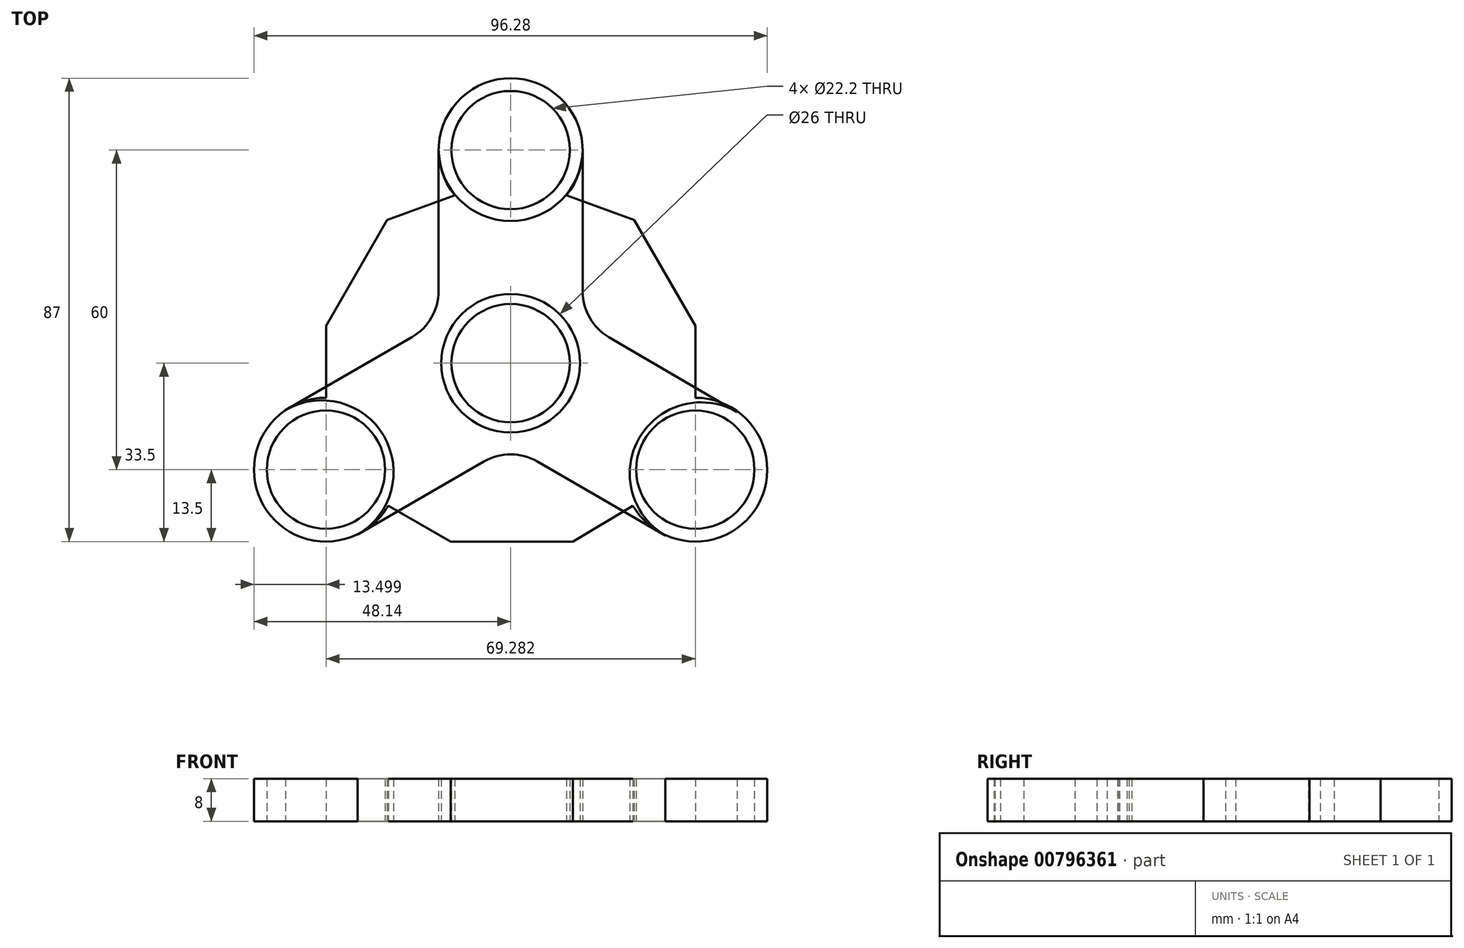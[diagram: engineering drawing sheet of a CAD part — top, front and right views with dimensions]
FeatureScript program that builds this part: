
annotation { "Feature Type Name" : "Feature", "Feature Type Description" : "" }
export const myFeature = defineFeature(function(context is Context, id is Id, definition is map)
    precondition{}
    {
        {
            var Q0;
            Q0=qCreatedBy(makeId("Top.planeOp"),FACE);
            var sketch = newSketch(context, id + "F0", { "sketchPlane" : qUnion([Q0])});
            skCircle(sketch, "E0", {"center": v(0, 0) * mm, "radius": 13.5 * mm});
            skCircle(sketch, "E1", {"center": v(0, 40) * mm, "radius": 13.5 * mm});
            skCircle(sketch, "E2.1.0", {"center": v(-34.64, -20) * mm, "radius": 13.5 * mm});
            skCircle(sketch, "E2.2.0", {"center": v(34.64, -20) * mm, "radius": 13.5 * mm});
            skCircle(sketch, "E3", {"center": v(0, 40) * mm, "radius": 11.1 * mm});
            skCircle(sketch, "E4", {"center": v(34.64, -20) * mm, "radius": 11.1 * mm});
            skCircle(sketch, "E5", {"center": v(-34.64, -20) * mm, "radius": 11.1 * mm});
            skCircle(sketch, "E6", {"center": v(0, 0) * mm, "radius": 11.1 * mm});
            skLineSegment(sketch, "E7", {"start": v(-34.64, 7) * mm, "end": v(-23.17, 26.88) * mm});
            skLineSegment(sketch, "E8", {"start": v(23.17, 26.88) * mm, "end": v(34.64, 7) * mm});
            skLineSegment(sketch, "E9", {"start": v(-11.26, -33.5) * mm, "end": v(11.7, -33.5) * mm});
            skLineSegment(sketch, "E10", {"start": v(-34.64, 7) * mm, "end": v(-34.64, -6.5) * mm});
            skLineSegment(sketch, "E11", {"start": v(-22.95, -26.75) * mm, "end": v(-11.26, -33.5) * mm});
            skPoint(sketch, "E12.orphan", {"position": v(-46.33, -13.25) * mm});
            skLineSegment(sketch, "E13", {"start": v(34.64, 7) * mm, "end": v(34.64, -6.5) * mm});
            skLineSegment(sketch, "E14", {"start": v(22.95, -26.75) * mm, "end": v(11.7, -33.5) * mm});
            skPoint(sketch, "E15.orphan", {"position": v(34.64, -33.5) * mm});
            skLineSegment(sketch, "E16", {"start": v(-10.48, 31.49) * mm, "end": v(-23.17, 26.87) * mm});
            skPoint(sketch, "E17.orphan", {"position": v(-11.7, 46.75) * mm});
            skLineSegment(sketch, "E18", {"start": v(10.48, 31.49) * mm, "end": v(23.17, 26.88) * mm});
            skPoint(sketch, "E19.orphan", {"position": v(11.7, 46.75) * mm});
            skSolve(sketch);
        }
        {
            var Q0;
            Q0=qCreatedBy(makeId("Top.planeOp"),FACE);
            var sketch = newSketch(context, id + "F1", { "sketchPlane" : qUnion([Q0])});
            skLineSegment(sketch, "E20", {"start": v(-42.2, -8.78) * mm, "end": v(-18.5, 4.9) * mm});
            skLineSegment(sketch, "E21", {"start": v(-28.7, -32.16) * mm, "end": v(-5, -18.48) * mm});
            skLineSegment(sketch, "E22", {"start": v(18.46, 4.86) * mm, "end": v(42.5, -9.18) * mm});
            skLineSegment(sketch, "E23", {"start": v(29.04, -32.36) * mm, "end": v(5, -18.48) * mm});
            skLineSegment(sketch, "E24", {"start": v(-13.5, 40.18) * mm, "end": v(-13.5, 13.57) * mm});
            skLineSegment(sketch, "E25", {"start": v(13.5, 40.18) * mm, "end": v(13.5, 13.5) * mm});
            skPoint(sketch, "E26.orphan", {"position": v(-13.5, 0) * mm});
            skPoint(sketch, "E27.orphan", {"position": v(13.5, 0) * mm});
            skPoint(sketch, "E28.visualSharp", {"position": v(-13.5, 7.8) * mm});
            skArc(sketch, "E28.filletArc", {"start": v(-18.5, 4.9) * mm, "mid": v(-14.84, 8.57) * mm, "end": v(-13.5, 13.57) * mm});
            skPoint(sketch, "E29.visualSharp", {"position": v(13.5, 7.75) * mm});
            skArc(sketch, "E29.filletArc", {"start": v(13.5, 13.5) * mm, "mid": v(14.83, 8.51) * mm, "end": v(18.46, 4.86) * mm});
            skPoint(sketch, "E30.visualSharp", {"position": v(0, -15.59) * mm});
            skArc(sketch, "E30.filletArc", {"start": v(5, -18.48) * mm, "mid": v(0, -17.14) * mm, "end": v(-5, -18.48) * mm});
            skArc(sketch, "E31", {"start": v(-13.5, 40.18) * mm, "mid": v(0, 26.68) * mm, "end": v(13.5, 40.18) * mm});
            skPoint(sketch, "E31.third.point", {"position": v(0, 53.68) * mm});
            skPoint(sketch, "E31.third.point.positionSnap0", {"position": v(0, 40.18) * mm});
            skArc(sketch, "E32", {"start": v(42.5, -9.18) * mm, "mid": v(24.15, -14.02) * mm, "end": v(29.04, -32.36) * mm});
            skPoint(sketch, "E32.third.point", {"position": v(47.1, -27.85) * mm});
            skArc(sketch, "E33", {"start": v(-28.7, -32.16) * mm, "mid": v(-23.77, -13.72) * mm, "end": v(-42.2, -8.78) * mm});
            skPoint(sketch, "E33.third.point", {"position": v(-48.06, -25.32) * mm});
            skPoint(sketch, "E33.third.point.positionSnap0", {"position": v(-16.85, -25.32) * mm});
            skCircle(sketch, "E34", {"center": v(0, 0) * mm, "radius": 13 * mm});
            skSolve(sketch);
        }
        {
            var Q0;
            Q0=makeQuery(id+"F1.imprint","IMPRINT",FACE,{"disambiguationData":[TD([[makeQuery(id+"F1.imprint","IMPRINT",EDGE,{"derivedFrom":sQuery(id+"F1.wireOp",EDGE,"E20")}),-1.0]])]});
            extrude(context, id + "F2", {"entities" : qUnion([Q0]), "endBound" : BoundingType.SYMMETRIC, "depth" : 8 * mm, "offsetDistance" : 25 * mm});
        }
        {
            var Q0;
            Q0=makeQuery(id+"F0.imprint","IMPRINT",FACE,{"disambiguationData":[TD([[makeQuery(id+"F0.imprint","IMPRINT",EDGE,{"derivedFrom":sQuery(id+"F0.wireOp",EDGE,"E1")}),1.0]])]});
            var Q1;
            Q1=makeQuery(id+"F0.imprint","IMPRINT",FACE,{"disambiguationData":[TD([[makeQuery(id+"F0.imprint","IMPRINT",EDGE,{"derivedFrom":sQuery(id+"F0.wireOp",EDGE,"E2.2.0")}),1.0]])]});
            var Q2;
            Q2=makeQuery(id+"F0.imprint","IMPRINT",FACE,{"disambiguationData":[TD([[makeQuery(id+"F0.imprint","IMPRINT",EDGE,{"derivedFrom":sQuery(id+"F0.wireOp",EDGE,"E2.1.0")}),1.0]])]});
            var Q3;
            Q3=makeQuery(id+"F0.imprint","IMPRINT",FACE,{"disambiguationData":[TD([[makeQuery(id+"F0.imprint","IMPRINT",EDGE,{"derivedFrom":sQuery(id+"F0.wireOp",EDGE,"E0")}),1.0]])]});
            var Q4;
            Q4=makeQuery(id+"F0.imprint","IMPRINT",FACE,{"disambiguationData":[TD([[makeQuery(id+"F0.imprint","IMPRINT",EDGE,{"derivedFrom":sQuery(id+"F0.wireOp",EDGE,"E0")}),-1.0]])]});
            extrude(context, id + "F3", {"entities" : qUnion([Q0, Q1, Q2, Q3, Q4]), "endBound" : BoundingType.SYMMETRIC, "depth" : 8 * mm, "offsetDistance" : 25 * mm});
        }
    });
